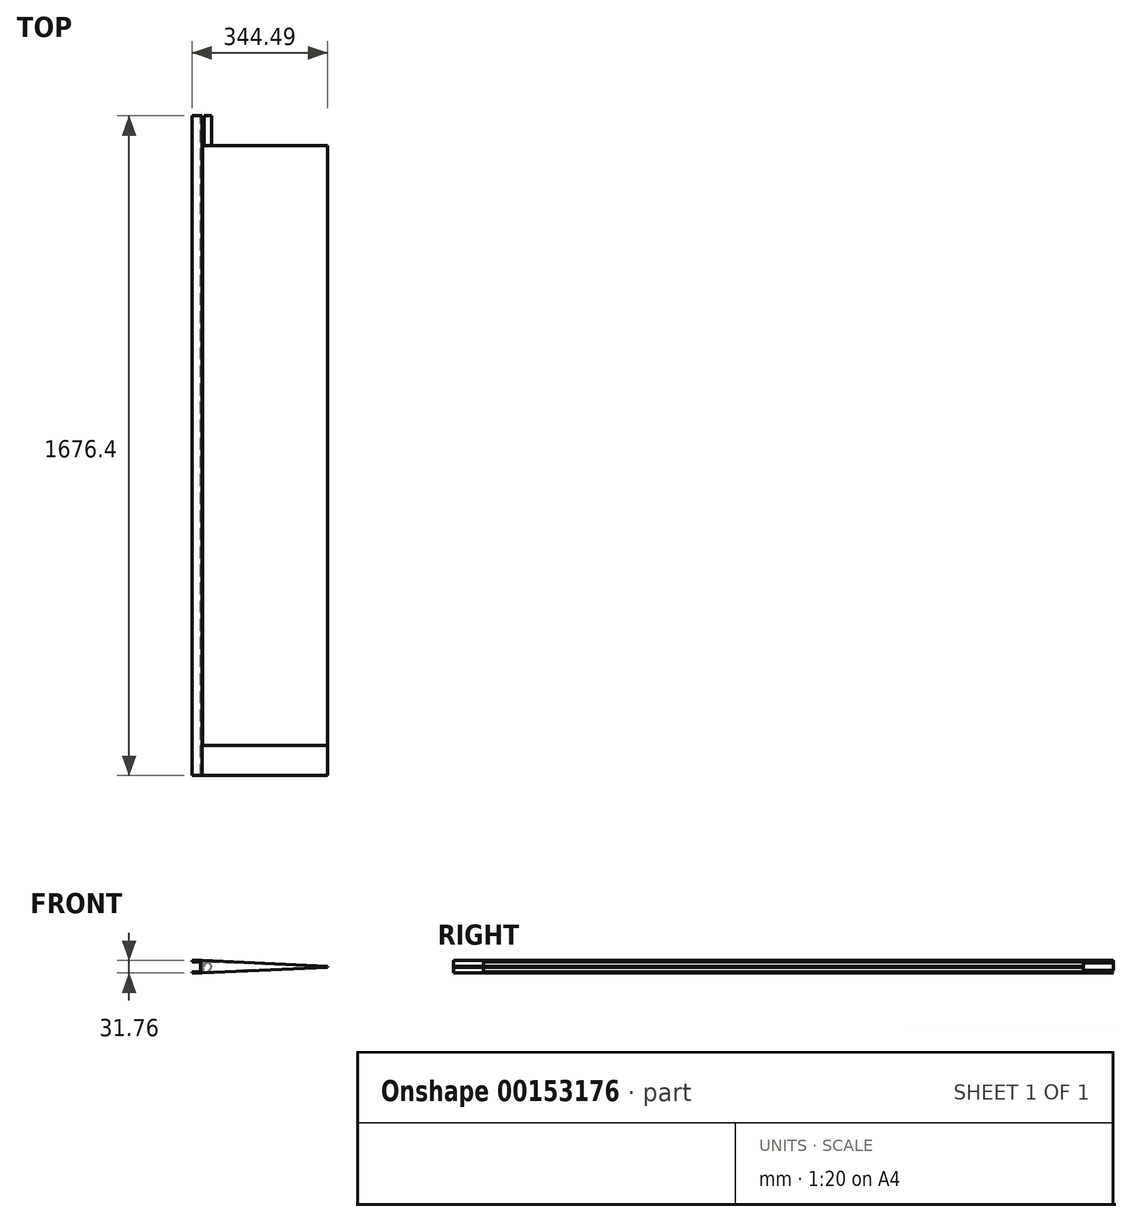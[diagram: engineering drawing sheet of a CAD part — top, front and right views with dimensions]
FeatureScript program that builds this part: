
annotation { "Feature Type Name" : "Feature", "Feature Type Description" : "" }
export const myFeature = defineFeature(function(context is Context, id is Id, definition is map)
    precondition{}
    {
        {
            var Q0;
            Q0=qCreatedBy(makeId("Front.planeOp"),FACE);
            var sketch = newSketch(context, id + "F0", { "sketchPlane" : qUnion([Q0])});
            skArc(sketch, "E0", {"start": v(0.46, 12.7) * mm, "mid": v(-12.7, 0) * mm, "end": v(0.46, -12.7) * mm});
            skCircle(sketch, "E1", {"center": v(0, 0) * mm, "radius": 9.53 * mm});
            skLineSegment(sketch, "E2", {"start": v(0.46, 12.7) * mm, "end": v(304.8, 1.59) * mm});
            skLineSegment(sketch, "E3", {"start": v(304.8, 1.59) * mm, "end": v(304.8, -1.59) * mm});
            skLineSegment(sketch, "E4", {"start": v(304.8, -1.59) * mm, "end": v(0.46, -12.7) * mm});
            skLineSegment(sketch, "E5", {"start": v(304.8, 0) * mm, "end": v(0, 0) * mm, "construction": true});
            skSolve(sketch);
        }
        {
            var Q0;
            Q0=makeQuery(id+"F0.imprint","IMPRINT",FACE,{"disambiguationData":[TD([[makeQuery(id+"F0.imprint","IMPRINT",EDGE,{"derivedFrom":sQuery(id+"F0.wireOp",EDGE,"E0")}),1.0]])]});
            var Q1;
            Q1=makeQuery(id+"F0.imprint","IMPRINT",FACE,{"disambiguationData":[TD([[makeQuery(id+"F0.imprint","IMPRINT",EDGE,{"derivedFrom":sQuery(id+"F0.wireOp",EDGE,"E1")}),1.0]])]});
            extrude(context, id + "F1", {"entities" : qUnion([Q0, Q1]), "endBound" : BoundingType.SYMMETRIC, "depth" : 1524 * mm});
        }
        {
            var Q0;
            Q0=makeQuery(id+"F0.imprint","IMPRINT",FACE,{"disambiguationData":[TD([[makeQuery(id+"F0.imprint","IMPRINT",EDGE,{"derivedFrom":sQuery(id+"F0.wireOp",EDGE,"E1")}),1.0]])]});
            extrude(context, id + "F2", {"entities" : qUnion([Q0]), "operationType" : NewBodyOperationType.ADD, "endBound" : BoundingType.SYMMETRIC, "depth" : 1676.4 * mm});
        }
        {
            var Q0;
            Q0=qCreatedBy(makeId("Front.planeOp"),FACE);
            var sketch = newSketch(context, id + "F3", { "sketchPlane" : qUnion([Q0])});
            skLineSegment(sketch, "E6.bottom", {"start": v(-14.29, 15.88) * mm, "end": v(-39.69, 15.87) * mm});
            skLineSegment(sketch, "E6.top", {"start": v(-14.29, -15.88) * mm, "end": v(-39.69, -15.88) * mm});
            skLineSegment(sketch, "E6.left", {"start": v(-14.29, 15.88) * mm, "end": v(-14.29, -15.88) * mm});
            skLineSegment(sketch, "E6.right", {"start": v(-39.69, 15.87) * mm, "end": v(-39.69, 12.7) * mm});
            skLineSegment(sketch, "E7", {"start": v(0, 0) * mm, "end": v(-14.29, 0) * mm, "construction": true});
            skLineSegment(sketch, "E8.bottom", {"start": v(-39.69, 12.7) * mm, "end": v(-17.46, 12.7) * mm});
            skLineSegment(sketch, "E8.top", {"start": v(-39.69, -12.7) * mm, "end": v(-17.46, -12.7) * mm});
            skLineSegment(sketch, "E8.right", {"start": v(-17.46, 12.7) * mm, "end": v(-17.46, -12.7) * mm});
            skLineSegment(sketch, "E9.trimOffspring", {"start": v(-39.69, -12.7) * mm, "end": v(-39.69, -15.88) * mm});
            skLineSegment(sketch, "E10", {"start": v(-14.29, 0) * mm, "end": v(-17.46, 0) * mm, "construction": true});
            skSolve(sketch);
        }
        {
            var Q0;
            Q0 = qSketchRegion(id + "F3", true);
            extrude(context, id + "F4", {"entities" : qUnion([Q0]), "endBound" : BoundingType.SYMMETRIC, "depth" : 1676.4 * mm});
        }
        {
            var Q0;
            Q0=makeQuery(id+"F1.opExtrude","CAP_FACE",FACE,{"disambiguationData":[OSD([sQuery(id+"F0.wireOp",EDGE,"E0"),sQuery(id+"F0.wireOp",EDGE,"E2"),sQuery(id+"F0.wireOp",EDGE,"E3"),sQuery(id+"F0.wireOp",EDGE,"E4")])],"isStart":false});
            var sketch = newSketch(context, id + "F5", { "sketchPlane" : qUnion([Q0])});
            skCircle(sketch, "E11.0", {"center": v(0, 0) * mm, "radius": 9.53 * mm});
            skLineSegment(sketch, "E11.3", {"start": v(304.8, 1.59) * mm, "end": v(304.8, -1.59) * mm});
            skLineSegment(sketch, "E12", {"start": v(304.8, 1.59) * mm, "end": v(-14.29, 15.88) * mm});
            skLineSegment(sketch, "E13", {"start": v(304.8, -1.59) * mm, "end": v(-14.29, -15.88) * mm});
            skLineSegment(sketch, "E14.0", {"start": v(-14.29, 15.88) * mm, "end": v(-14.29, -15.88) * mm});
            skSolve(sketch);
        }
        {
            var Q0;
            Q0 = qSketchRegion(id + "F5", true);
            extrude(context, id + "F6", {"entities" : qUnion([Q0]), "operationType" : NewBodyOperationType.ADD, "depth" : 76.2 * mm});
        }
    });
